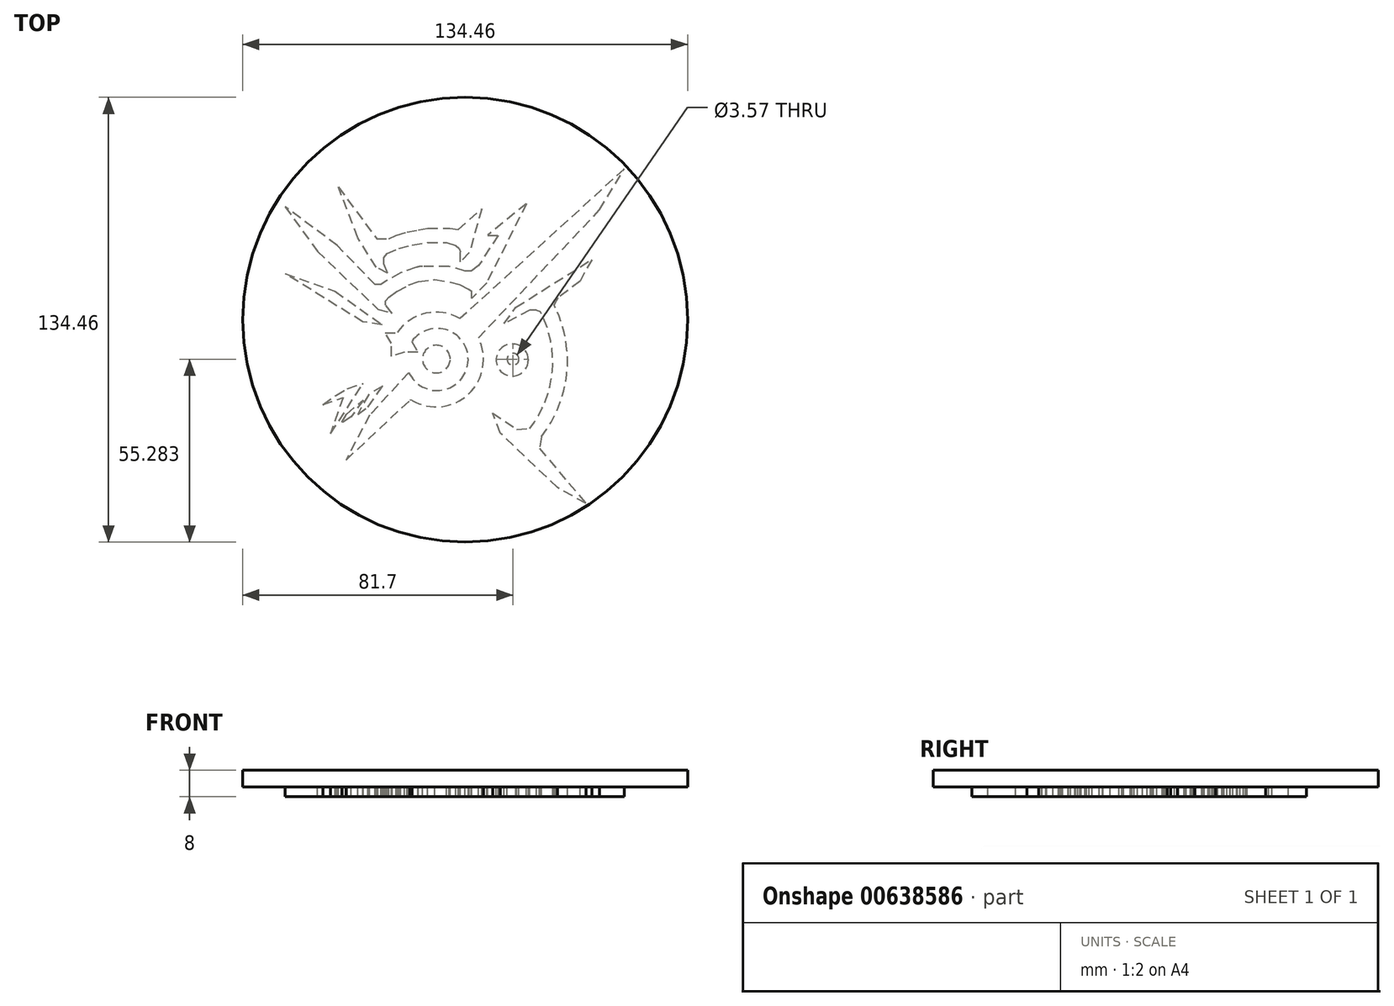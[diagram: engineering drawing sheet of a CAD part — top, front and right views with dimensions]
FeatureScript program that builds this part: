
annotation { "Feature Type Name" : "Feature", "Feature Type Description" : "" }
export const myFeature = defineFeature(function(context is Context, id is Id, definition is map)
    precondition{}
    {
        {
            var Q0;
            Q0=qCreatedBy(makeId("Top.planeOp"),FACE);
            var sketch = newSketch(context, id + "F0", { "sketchPlane" : qUnion([Q0])});
            skLineSegment(sketch, "E0", {"start": v(-35.95, -42.39) * mm, "end": v(-16.66, -24.32) * mm});
            skArc(sketch, "E1", {"start": v(-16.02, -24.39) * mm, "mid": v(1.05, -22.44) * mm, "end": v(3.96, -5.5) * mm});
            skPoint(sketch, "E1.first.point", {"position": v(-16.02, -24.39) * mm});
            skPoint(sketch, "E1.second.point", {"position": v(-12.4, 1.82) * mm});
            skPoint(sketch, "E1.third.point", {"position": v(5.54, -12.03) * mm});
            skArc(sketch, "E2", {"start": v(-17, -15.97) * mm, "mid": v(0.88, -12.92) * mm, "end": v(-16.1, -6.56) * mm});
            skPoint(sketch, "E2.first.point", {"position": v(-10.99, -2.98) * mm});
            skPoint(sketch, "E2.second.point", {"position": v(0.9, -11.4) * mm});
            skPoint(sketch, "E2.third.point", {"position": v(-9.88, -21.32) * mm});
            skLineSegment(sketch, "E3", {"start": v(-16.1, -6.56) * mm, "end": v(-14.3, -9.75) * mm});
            skLineSegment(sketch, "E4", {"start": v(-14.3, -9.75) * mm, "end": v(-18.3, -9.75) * mm});
            skLineSegment(sketch, "E5", {"start": v(-18.3, -9.75) * mm, "end": v(-22.24, -11.09) * mm});
            skLineSegment(sketch, "E6", {"start": v(-22.24, -11.09) * mm, "end": v(-22.24, -7.15) * mm});
            skLineSegment(sketch, "E7", {"start": v(-22.24, -7.15) * mm, "end": v(-24.13, -3.93) * mm});
            skLineSegment(sketch, "E8", {"start": v(-24.13, -3.93) * mm, "end": v(-20.58, -3.93) * mm});
            skLineSegment(sketch, "E9", {"start": v(-17, -15.97) * mm, "end": v(-28.85, -28.87) * mm});
            skLineSegment(sketch, "E10", {"start": v(-28.85, -28.87) * mm, "end": v(-35.95, -42.39) * mm});
            skCircle(sketch, "E11", {"center": v(-8.7, -11.89) * mm, "radius": 4.19 * mm});
            skPoint(sketch, "E11.first.point", {"position": v(-8.47, -7.7) * mm});
            skPoint(sketch, "E11.second.point", {"position": v(-4.53, -12.35) * mm});
            skPoint(sketch, "E11.third.point", {"position": v(-7.76, -15.97) * mm});
            skLineSegment(sketch, "E12", {"start": v(-32.47, -28.56) * mm, "end": v(-29.32, -26.44) * mm});
            skLineSegment(sketch, "E13", {"start": v(-29.32, -26.44) * mm, "end": v(-25, -20.14) * mm});
            skLineSegment(sketch, "E14", {"start": v(-25, -20.14) * mm, "end": v(-29.17, -22.58) * mm});
            skLineSegment(sketch, "E15", {"start": v(-29.17, -22.58) * mm, "end": v(-32.47, -28.56) * mm});
            skLineSegment(sketch, "E16", {"start": v(-30.82, -24.23) * mm, "end": v(-34.44, -29.43) * mm});
            skPoint(sketch, "E16.startSnap0", {"position": v(-30.82, -25.57) * mm});
            skLineSegment(sketch, "E17", {"start": v(-34.44, -29.43) * mm, "end": v(-37.2, -31.08) * mm});
            skLineSegment(sketch, "E18", {"start": v(-37.2, -31.08) * mm, "end": v(-35.8, -28.56) * mm});
            skLineSegment(sketch, "E19", {"start": v(-35.8, -28.56) * mm, "end": v(-30.82, -24.23) * mm});
            skLineSegment(sketch, "E20", {"start": v(-40.66, -34.46) * mm, "end": v(-30.82, -19.27) * mm});
            skLineSegment(sketch, "E21", {"start": v(-43.02, -25.65) * mm, "end": v(-36.92, -23.52) * mm});
            skPoint(sketch, "E21.endSnap0", {"position": v(-36.92, -22.46) * mm});
            skLineSegment(sketch, "E22", {"start": v(-36.92, -23.52) * mm, "end": v(-40.66, -34.46) * mm});
            skLineSegment(sketch, "E23", {"start": v(3.96, -5.5) * mm, "end": v(40.64, 33.23) * mm});
            skLineSegment(sketch, "E24", {"start": v(40.64, 33.23) * mm, "end": v(48.04, 45.57) * mm});
            skLineSegment(sketch, "E25", {"start": v(48.04, 45.57) * mm, "end": v(-1.54, 0.32) * mm});
            skArc(sketch, "E26.trimOffspring", {"start": v(-1.54, 0.32) * mm, "mid": v(-11.9, 1.94) * mm, "end": v(-20.58, -3.93) * mm});
            skCircle(sketch, "E27", {"center": v(14.23, -12.17) * mm, "radius": 4.85 * mm});
            skPoint(sketch, "E27.first.point", {"position": v(14.34, -7.32) * mm});
            skPoint(sketch, "E27.second.point", {"position": v(19.08, -12.02) * mm});
            skPoint(sketch, "E27.third.point", {"position": v(15.8, -16.76) * mm});
            skCircle(sketch, "E28", {"center": v(14.47, -11.95) * mm, "radius": 1.79 * mm});
            skPoint(sketch, "E28.first.point", {"position": v(13.28, -13.28) * mm});
            skPoint(sketch, "E28.second.point", {"position": v(14.64, -10.17) * mm});
            skPoint(sketch, "E28.third.point", {"position": v(16.07, -12.75) * mm});
            skPoint(sketch, "E29.first.point", {"position": v(21.51, 2.91) * mm});
            skPoint(sketch, "E29.second.point", {"position": v(25.81, -16.18) * mm});
            skPoint(sketch, "E29.third.point", {"position": v(19.45, -32.93) * mm});
            skLineSegment(sketch, "E30", {"start": v(21.51, 2.91) * mm, "end": v(19.55, 2.91) * mm});
            skLineSegment(sketch, "E31", {"start": v(19.55, 2.91) * mm, "end": v(11.78, -1.2) * mm});
            skLineSegment(sketch, "E32", {"start": v(11.78, -1.2) * mm, "end": v(15.33, 3.75) * mm});
            skLineSegment(sketch, "E33", {"start": v(15.33, 3.75) * mm, "end": v(38.26, 18.17) * mm});
            skLineSegment(sketch, "E34", {"start": v(38.26, 18.17) * mm, "end": v(34.7, 11.7) * mm});
            skLineSegment(sketch, "E35", {"start": v(34.7, 11.7) * mm, "end": v(27.97, 6.56) * mm});
            skLineSegment(sketch, "E36", {"start": v(27.97, 6.56) * mm, "end": v(26.94, 4.5) * mm});
            skPoint(sketch, "E37.second.point", {"position": v(30.21, -19.64) * mm});
            skPoint(sketch, "E37.third.point", {"position": v(23, -35.37) * mm});
            skLineSegment(sketch, "E38", {"start": v(23, -35.37) * mm, "end": v(22.47, -38.93) * mm});
            skLineSegment(sketch, "E39", {"start": v(22.47, -38.93) * mm, "end": v(36.48, -55.55) * mm});
            skLineSegment(sketch, "E40", {"start": v(36.48, -55.55) * mm, "end": v(27.87, -50.72) * mm});
            skLineSegment(sketch, "E41", {"start": v(27.87, -50.72) * mm, "end": v(10.65, -34.34) * mm});
            skLineSegment(sketch, "E42", {"start": v(10.65, -34.34) * mm, "end": v(8.31, -28.16) * mm});
            skLineSegment(sketch, "E43", {"start": v(8.31, -28.16) * mm, "end": v(15.61, -33.12) * mm});
            skLineSegment(sketch, "E44", {"start": v(15.61, -33.12) * mm, "end": v(19.45, -32.93) * mm});
            skArc(sketch, "E45.trimOffspring", {"start": v(23, -35.37) * mm, "mid": v(30.7, -16.54) * mm, "end": v(27.33, 3.51) * mm});
            skLineSegment(sketch, "E46", {"start": v(-43.02, -25.65) * mm, "end": v(-39.08, -22.87) * mm});
            skLineSegment(sketch, "E47", {"start": v(-39.08, -22.87) * mm, "end": v(-35.58, -20.83) * mm});
            skLineSegment(sketch, "E48", {"start": v(-35.58, -20.83) * mm, "end": v(-30.82, -19.27) * mm});
            skArc(sketch, "E49", {"start": v(19.45, -32.93) * mm, "mid": v(26.31, -15.67) * mm, "end": v(22.66, 2.55) * mm});
            skPoint(sketch, "E49.second.point", {"position": v(24.05, -0.43) * mm});
            skPoint(sketch, "E49.third.point", {"position": v(26.44, -11.9) * mm});
            skLineSegment(sketch, "E50", {"start": v(21.51, 2.91) * mm, "end": v(22.66, 2.55) * mm});
            skLineSegment(sketch, "E51", {"start": v(18.54, 35.08) * mm, "end": v(6.52, 11.16) * mm});
            skLineSegment(sketch, "E52", {"start": v(6.52, 11.16) * mm, "end": v(1.97, 6.43) * mm});
            skLineSegment(sketch, "E53", {"start": v(1.97, 6.43) * mm, "end": v(1.97, 8.6) * mm});
            skLineSegment(sketch, "E54", {"start": v(-23.43, 14.06) * mm, "end": v(-24.51, 16.91) * mm});
            skLineSegment(sketch, "E55", {"start": v(-23.43, 14.06) * mm, "end": v(-26.9, 15.89) * mm});
            skLineSegment(sketch, "E56", {"start": v(-26.9, 15.89) * mm, "end": v(-32.43, 24.71) * mm});
            skLineSegment(sketch, "E57", {"start": v(-32.43, 24.71) * mm, "end": v(-38.3, 40.14) * mm});
            skLineSegment(sketch, "E58", {"start": v(-38.3, 40.14) * mm, "end": v(-26.73, 24.43) * mm});
            skLineSegment(sketch, "E59", {"start": v(-26.73, 24.43) * mm, "end": v(-23.43, 24.43) * mm});
            skLineSegment(sketch, "E60", {"start": v(-2.13, 27.22) * mm, "end": v(4.99, 33.48) * mm});
            skLineSegment(sketch, "E61", {"start": v(4.99, 33.48) * mm, "end": v(1.29, 20.27) * mm});
            skLineSegment(sketch, "E62", {"start": v(1.29, 20.27) * mm, "end": v(-1.4, 17.48) * mm});
            skLineSegment(sketch, "E63", {"start": v(-1.4, 17.48) * mm, "end": v(-1.4, 20.56) * mm});
            skLineSegment(sketch, "E64", {"start": v(-24.51, 16.91) * mm, "end": v(-24.51, 18.73) * mm});
            skLineSegment(sketch, "E65", {"start": v(-24.51, 18.73) * mm, "end": v(-23.6, 20.04) * mm});
            skLineSegment(sketch, "E66", {"start": v(-23.6, 20.04) * mm, "end": v(-20.01, 21.52) * mm});
            skLineSegment(sketch, "E67", {"start": v(-20.01, 21.52) * mm, "end": v(-16.03, 22.6) * mm});
            skLineSegment(sketch, "E68", {"start": v(-16.03, 22.6) * mm, "end": v(-11.3, 23.3) * mm});
            skLineSegment(sketch, "E69", {"start": v(-11.3, 23.3) * mm, "end": v(-5.66, 23.3) * mm});
            skLineSegment(sketch, "E70", {"start": v(-5.66, 23.3) * mm, "end": v(-2.87, 22.5) * mm});
            skLineSegment(sketch, "E71", {"start": v(-2.87, 22.5) * mm, "end": v(-1.85, 21.52) * mm});
            skLineSegment(sketch, "E72", {"start": v(-1.85, 21.52) * mm, "end": v(-1.4, 20.56) * mm});
            skLineSegment(sketch, "E73", {"start": v(-23.03, 24.43) * mm, "end": v(-20.87, 25.51) * mm});
            skLineSegment(sketch, "E74", {"start": v(-20.87, 25.51) * mm, "end": v(-17.56, 26.48) * mm});
            skLineSegment(sketch, "E75", {"start": v(-17.56, 26.48) * mm, "end": v(-14.1, 27.16) * mm});
            skLineSegment(sketch, "E76", {"start": v(-14.1, 27.16) * mm, "end": v(-11.3, 27.68) * mm});
            skLineSegment(sketch, "E77", {"start": v(-11.3, 27.68) * mm, "end": v(-7.6, 27.68) * mm});
            skLineSegment(sketch, "E78", {"start": v(-7.6, 27.68) * mm, "end": v(-4.58, 27.68) * mm});
            skLineSegment(sketch, "E79", {"start": v(-4.58, 27.68) * mm, "end": v(-2.13, 27.22) * mm});
            skLineSegment(sketch, "E80", {"start": v(18.54, 35.08) * mm, "end": v(6.87, 25.51) * mm});
            skLineSegment(sketch, "E81", {"start": v(6.87, 25.51) * mm, "end": v(10, 25.51) * mm});
            skLineSegment(sketch, "E82", {"start": v(10, 25.51) * mm, "end": v(4.02, 16.34) * mm});
            skLineSegment(sketch, "E83", {"start": v(4.02, 16.34) * mm, "end": v(1.86, 14.75) * mm});
            skLineSegment(sketch, "E84", {"start": v(1.86, 14.75) * mm, "end": v(0, 14.75) * mm});
            skLineSegment(sketch, "E85", {"start": v(0, 14.75) * mm, "end": v(-2.69, 15.5) * mm});
            skLineSegment(sketch, "E86", {"start": v(-2.69, 15.5) * mm, "end": v(-4.92, 16.13) * mm});
            skLineSegment(sketch, "E87", {"start": v(-4.92, 16.13) * mm, "end": v(-12.86, 16.13) * mm});
            skLineSegment(sketch, "E88", {"start": v(-13.7, 16.13) * mm, "end": v(-13.74, 16.1) * mm});
            skLineSegment(sketch, "E89", {"start": v(-14.8, 15.8) * mm, "end": v(-19.5, 14.19) * mm});
            skLineSegment(sketch, "E90", {"start": v(-19.5, 14.19) * mm, "end": v(-23.83, 11.73) * mm});
            skLineSegment(sketch, "E91", {"start": v(-23.83, 11.73) * mm, "end": v(-25.48, 10.6) * mm});
            skLineSegment(sketch, "E92", {"start": v(-25.48, 10.6) * mm, "end": v(-27.25, 10.6) * mm});
            skLineSegment(sketch, "E93", {"start": v(-27.25, 10.6) * mm, "end": v(-38.63, 22.44) * mm});
            skLineSegment(sketch, "E94", {"start": v(-38.63, 22.44) * mm, "end": v(-54.44, 34.17) * mm});
            skLineSegment(sketch, "E95", {"start": v(-54.44, 34.17) * mm, "end": v(-44.61, 20.67) * mm});
            skLineSegment(sketch, "E96", {"start": v(-44.61, 20.67) * mm, "end": v(-26.33, 3.13) * mm});
            skLineSegment(sketch, "E97", {"start": v(-26.33, 3.13) * mm, "end": v(-22.06, 1.93) * mm});
            skLineSegment(sketch, "E98", {"start": v(-22.06, 1.93) * mm, "end": v(-24.06, 4.38) * mm});
            skLineSegment(sketch, "E99", {"start": v(-24.06, 4.38) * mm, "end": v(-24.06, 5.7) * mm});
            skLineSegment(sketch, "E100", {"start": v(-24.06, 5.7) * mm, "end": v(-23.03, 6.89) * mm});
            skLineSegment(sketch, "E101", {"start": v(-23.03, 6.89) * mm, "end": v(-20.47, 8.65) * mm});
            skLineSegment(sketch, "E102", {"start": v(-20.47, 8.65) * mm, "end": v(-17, 10.48) * mm});
            skLineSegment(sketch, "E103", {"start": v(-17, 10.48) * mm, "end": v(-14.1, 11.58) * mm});
            skLineSegment(sketch, "E104", {"start": v(-14.1, 11.58) * mm, "end": v(-9.2, 12.13) * mm});
            skLineSegment(sketch, "E105", {"start": v(-9.2, 12.13) * mm, "end": v(-4.64, 11.45) * mm});
            skLineSegment(sketch, "E106", {"start": v(-4.64, 11.45) * mm, "end": v(-1.7, 10.62) * mm});
            skLineSegment(sketch, "E107", {"start": v(-1.7, 10.62) * mm, "end": v(1.15, 9.19) * mm});
            skLineSegment(sketch, "E108", {"start": v(1.15, 9.19) * mm, "end": v(1.97, 8.6) * mm});
            skLineSegment(sketch, "E109", {"start": v(-25.08, -1.52) * mm, "end": v(-30.92, -0.64) * mm});
            skLineSegment(sketch, "E110", {"start": v(-30.92, -0.64) * mm, "end": v(-54.44, 13.94) * mm});
            skLineSegment(sketch, "E111", {"start": v(-54.44, 13.94) * mm, "end": v(-39.26, 8.6) * mm});
            skLineSegment(sketch, "E112", {"start": v(-39.26, 8.6) * mm, "end": v(-25.08, -1.52) * mm});
            skPoint(sketch, "E113.orphan", {"position": v(-1.89, 0) * mm});
            skLineSegment(sketch, "E114", {"start": v(-16.02, -24.39) * mm, "end": v(-16.66, -24.32) * mm});
            skLineSegment(sketch, "E115", {"start": v(-23.43, 24.43) * mm, "end": v(-23.03, 24.43) * mm});
            skCircle(sketch, "E116", {"center": v(0, 0) * mm, "radius": 67.23 * mm});
            skPoint(sketch, "E117", {"position": v(0, 45.57) * mm});
            skLineSegment(sketch, "E118", {"start": v(27.33, 3.51) * mm, "end": v(26.94, 4.5) * mm});
            skArc(sketch, "E119.filletArc", {"start": v(-12.86, 16.13) * mm, "mid": v(-13.84, 16.04) * mm, "end": v(-14.8, 15.8) * mm});
            skSolve(sketch);
        }
        {
            var Q0;
            Q0=makeQuery(id+"F0.imprint","IMPRINT",FACE,{"disambiguationData":[TD([[makeQuery(id+"F0.imprint","IMPRINT",EDGE,{"derivedFrom":sQuery(id+"F0.wireOp",EDGE,"E51")}),-1.0]])]});
            var Q1;
            Q1=makeQuery(id+"F0.imprint","IMPRINT",FACE,{"disambiguationData":[TD([[makeQuery(id+"F0.imprint","IMPRINT",EDGE,{"derivedFrom":sQuery(id+"F0.wireOp",EDGE,"E54")}),1.0]])]});
            var Q2;
            Q2=makeQuery(id+"F0.imprint","IMPRINT",FACE,{"disambiguationData":[TD([[makeQuery(id+"F0.imprint","IMPRINT",EDGE,{"derivedFrom":sQuery(id+"F0.wireOp",EDGE,"E109")}),-1.0]])]});
            var Q3;
            Q3=makeQuery(id+"F0.imprint","IMPRINT",FACE,{"disambiguationData":[TD([[makeQuery(id+"F0.imprint","IMPRINT",EDGE,{"derivedFrom":sQuery(id+"F0.wireOp",EDGE,"E20")}),1.0]])]});
            var Q4;
            Q4=makeQuery(id+"F0.imprint","IMPRINT",FACE,{"disambiguationData":[TD([[makeQuery(id+"F0.imprint","IMPRINT",EDGE,{"derivedFrom":sQuery(id+"F0.wireOp",EDGE,"E16")}),-1.0]])]});
            var Q5;
            Q5=makeQuery(id+"F0.imprint","IMPRINT",FACE,{"disambiguationData":[TD([[makeQuery(id+"F0.imprint","IMPRINT",EDGE,{"derivedFrom":sQuery(id+"F0.wireOp",EDGE,"E12")}),1.0]])]});
            var Q6;
            Q6=makeQuery(id+"F0.imprint","IMPRINT",FACE,{"disambiguationData":[TD([[makeQuery(id+"F0.imprint","IMPRINT",EDGE,{"derivedFrom":sQuery(id+"F0.wireOp",EDGE,"E0")}),1.0]])]});
            var Q7;
            Q7=makeQuery(id+"F0.imprint","IMPRINT",FACE,{"disambiguationData":[TD([[makeQuery(id+"F0.imprint","IMPRINT",EDGE,{"derivedFrom":sQuery(id+"F0.wireOp",EDGE,"E11")}),1.0]])]});
            var Q8;
            Q8=makeQuery(id+"F0.imprint","IMPRINT",FACE,{"disambiguationData":[TD([[makeQuery(id+"F0.imprint","IMPRINT",EDGE,{"derivedFrom":sQuery(id+"F0.wireOp",EDGE,"E27")}),1.0]])]});
            var Q9;
            Q9=makeQuery(id+"F0.imprint","IMPRINT",FACE,{"disambiguationData":[TD([[makeQuery(id+"F0.imprint","IMPRINT",EDGE,{"derivedFrom":sQuery(id+"F0.wireOp",EDGE,"E30")}),-1.0]])]});
            extrude(context, id + "F1", {"entities" : qUnion([Q0, Q1, Q2, Q3, Q4, Q5, Q6, Q7, Q8, Q9]), "oppositeDirection" : true, "depth" : 3 * mm, "offsetDistance" : 25 * mm});
        }
        {
            var Q0;
            Q0=makeQuery(id+"F0.imprint","IMPRINT",FACE,{"disambiguationData":[TD([[makeQuery(id+"F0.imprint","IMPRINT",EDGE,{"derivedFrom":sQuery(id+"F0.wireOp",EDGE,"E0")}),1.0]])]});
            var Q1;
            Q1=makeQuery(id+"F0.imprint","IMPRINT",FACE,{"disambiguationData":[TD([[makeQuery(id+"F0.imprint","IMPRINT",EDGE,{"derivedFrom":sQuery(id+"F0.wireOp",EDGE,"E12")}),1.0]])]});
            var Q2;
            Q2=makeQuery(id+"F0.imprint","IMPRINT",FACE,{"disambiguationData":[TD([[makeQuery(id+"F0.imprint","IMPRINT",EDGE,{"derivedFrom":sQuery(id+"F0.wireOp",EDGE,"E16")}),-1.0]])]});
            var Q3;
            Q3=makeQuery(id+"F0.imprint","IMPRINT",FACE,{"disambiguationData":[TD([[makeQuery(id+"F0.imprint","IMPRINT",EDGE,{"derivedFrom":sQuery(id+"F0.wireOp",EDGE,"E20")}),1.0]])]});
            var Q4;
            Q4=makeQuery(id+"F0.imprint","IMPRINT",FACE,{"disambiguationData":[TD([[makeQuery(id+"F0.imprint","IMPRINT",EDGE,{"derivedFrom":sQuery(id+"F0.wireOp",EDGE,"E109")}),-1.0]])]});
            var Q5;
            Q5=makeQuery(id+"F0.imprint","IMPRINT",FACE,{"disambiguationData":[TD([[makeQuery(id+"F0.imprint","IMPRINT",EDGE,{"derivedFrom":sQuery(id+"F0.wireOp",EDGE,"E51")}),-1.0]])]});
            var Q6;
            Q6=makeQuery(id+"F0.imprint","IMPRINT",FACE,{"disambiguationData":[TD([[makeQuery(id+"F0.imprint","IMPRINT",EDGE,{"derivedFrom":sQuery(id+"F0.wireOp",EDGE,"E11")}),1.0]])]});
            var Q7;
            Q7=makeQuery(id+"F0.imprint","IMPRINT",FACE,{"disambiguationData":[TD([[makeQuery(id+"F0.imprint","IMPRINT",EDGE,{"derivedFrom":sQuery(id+"F0.wireOp",EDGE,"E27")}),1.0]])]});
            var Q8;
            Q8=makeQuery(id+"F0.imprint","IMPRINT",FACE,{"disambiguationData":[TD([[makeQuery(id+"F0.imprint","IMPRINT",EDGE,{"derivedFrom":sQuery(id+"F0.wireOp",EDGE,"E28")}),1.0]])]});
            var Q9;
            Q9=makeQuery(id+"F0.imprint","IMPRINT",FACE,{"disambiguationData":[TD([[makeQuery(id+"F0.imprint","IMPRINT",EDGE,{"derivedFrom":sQuery(id+"F0.wireOp",EDGE,"E54")}),1.0]])]});
            var Q10;
            Q10=makeQuery(id+"F0.imprint","IMPRINT",FACE,{"disambiguationData":[TD([[makeQuery(id+"F0.imprint","IMPRINT",EDGE,{"derivedFrom":sQuery(id+"F0.wireOp",EDGE,"E0")}),-1.0]])]});
            var Q11;
            Q11=makeQuery(id+"F0.imprint","IMPRINT",FACE,{"disambiguationData":[TD([[makeQuery(id+"F0.imprint","IMPRINT",EDGE,{"derivedFrom":sQuery(id+"F0.wireOp",EDGE,"E30")}),-1.0]])]});
            extrude(context, id + "F2", {"entities" : qUnion([Q0, Q1, Q2, Q3, Q4, Q5, Q6, Q7, Q8, Q9, Q10, Q11]), "depth" : 5 * mm, "offsetDistance" : 25 * mm});
        }
    });
